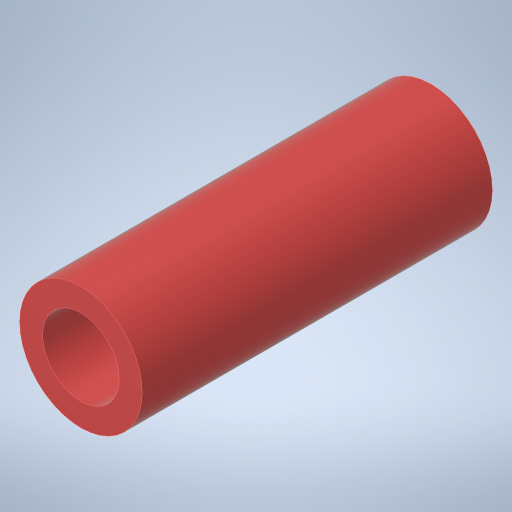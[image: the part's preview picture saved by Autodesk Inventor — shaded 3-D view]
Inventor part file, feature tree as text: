
AUTODESK INVENTOR PART (.ipt)
format: ipt  version: 2023.3 (Build 273359000, 359)  size: 233,472 bytes
history: native  units: in
note: dims shown in document units (in); Inventor stores cm internally (conversion verified against a paired STEP export)
features: extrude x1, sketch x1
ambient origin geometry x8: Origin, YZ Plane, XZ Plane, XY Plane, X Axis, Y Axis, Z Axis, Center Point
bodies: Solid1 (feature_tree)
feature tree (2):
  extrude  "Extrusion1"  [1 undecoded]
  sketch  "Sketch1"  dims[d3=0.0in]
note: 1 required parameter value undecoded (feature->parameter linkage not recoverable at this tier; creation-order binding heuristic only, values carry confidence <= 0.55)
